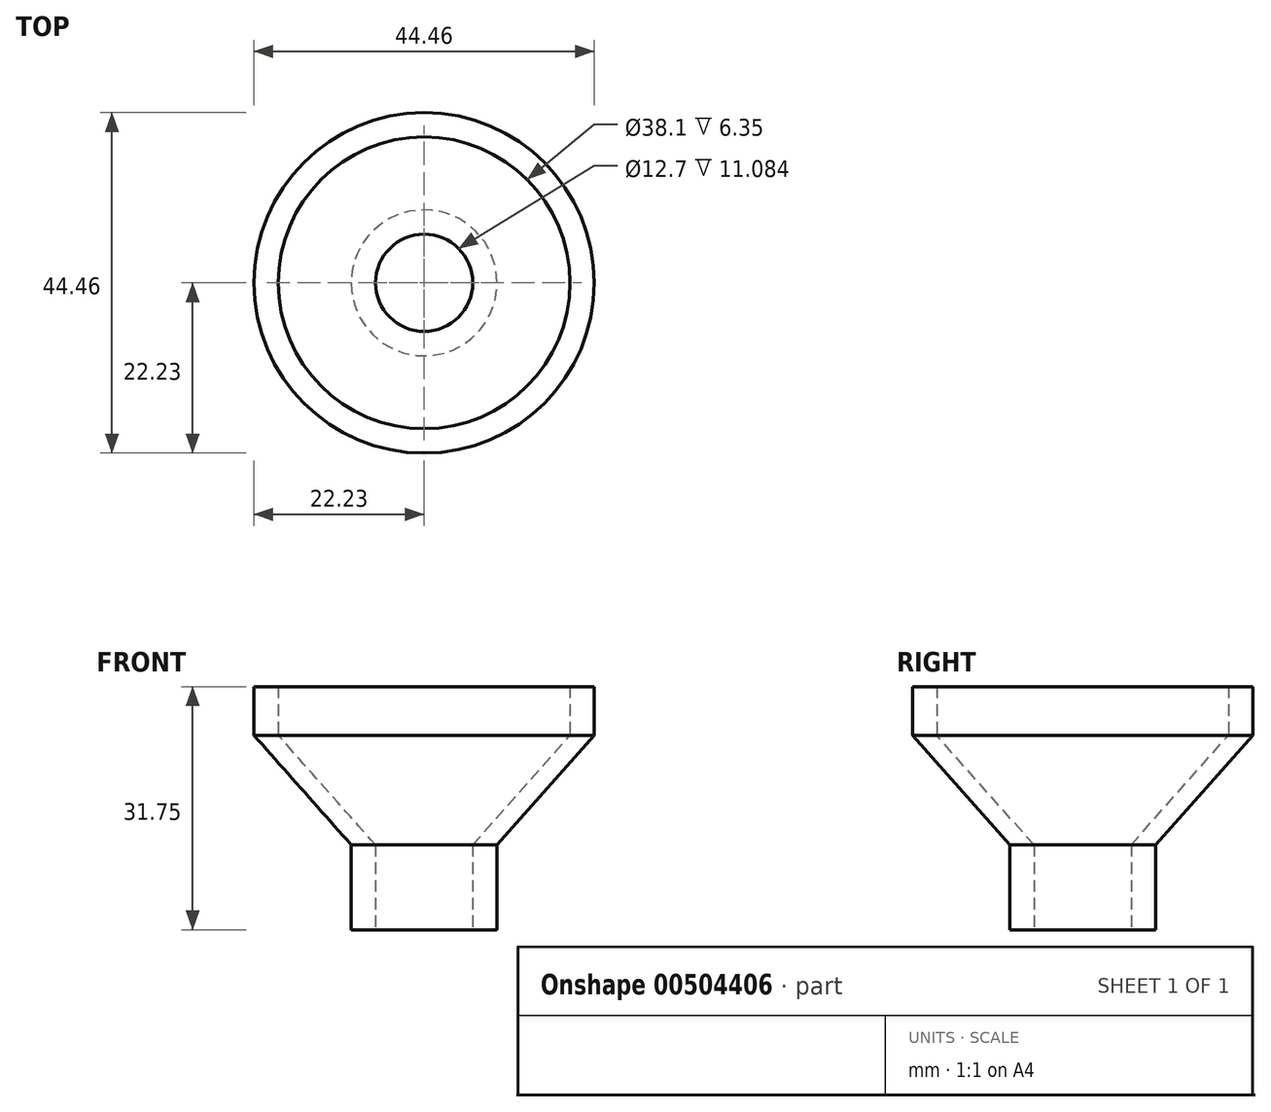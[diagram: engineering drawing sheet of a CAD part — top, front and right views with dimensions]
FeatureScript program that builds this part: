
annotation { "Feature Type Name" : "Feature", "Feature Type Description" : "" }
export const myFeature = defineFeature(function(context is Context, id is Id, definition is map)
    precondition{}
    {
        {
            var Q0;
            Q0=qCreatedBy(makeId("Right.planeOp"),FACE);
            var sketch = newSketch(context, id + "F0", { "sketchPlane" : qUnion([Q0])});
            skLineSegment(sketch, "E0.bottom", {"start": v(22.22, 6.35) * mm, "end": v(19.05, 6.35) * mm});
            skLineSegment(sketch, "E0.top", {"start": v(22.23, 0) * mm, "end": v(19.05, 0) * mm});
            skLineSegment(sketch, "E0.left", {"start": v(22.23, 6.35) * mm, "end": v(22.23, 0) * mm});
            skLineSegment(sketch, "E0.right", {"start": v(19.05, 6.35) * mm, "end": v(19.05, 0) * mm});
            skLineSegment(sketch, "E1.bottom", {"start": v(9.52, -14.32) * mm, "end": v(6.35, -14.32) * mm});
            skLineSegment(sketch, "E1.top", {"start": v(9.53, -25.4) * mm, "end": v(6.35, -25.4) * mm});
            skLineSegment(sketch, "E1.left", {"start": v(9.52, -14.32) * mm, "end": v(9.53, -25.4) * mm});
            skLineSegment(sketch, "E1.right", {"start": v(6.35, -14.32) * mm, "end": v(6.35, -25.4) * mm});
            skLineSegment(sketch, "E2", {"start": v(6.35, -25.4) * mm, "end": v(9.53, -25.4) * mm});
            skLineSegment(sketch, "E3", {"start": v(22.23, 0) * mm, "end": v(9.52, -14.32) * mm});
            skLineSegment(sketch, "E4", {"start": v(19.05, 0) * mm, "end": v(6.35, -14.32) * mm});
            skLineSegment(sketch, "E5", {"start": v(6.35, -25.4) * mm, "end": v(0, -25.4) * mm});
            skLineSegment(sketch, "E6", {"start": v(0, -25.4) * mm, "end": v(0, -18.22) * mm});
            skSolve(sketch);
        }
        {
            var Q0;
            Q0=makeQuery(id+"F0.imprint","IMPRINT",FACE,{"disambiguationData":[TD([[makeQuery(id+"F0.imprint","IMPRINT",EDGE,{"derivedFrom":sQuery(id+"F0.wireOp",EDGE,"E0.bottom")}),1.0]])]});
            var Q1;
            Q1=makeQuery(id+"F0.imprint","IMPRINT",FACE,{"disambiguationData":[TD([[makeQuery(id+"F0.imprint","IMPRINT",EDGE,{"derivedFrom":sQuery(id+"F0.wireOp",EDGE,"E0.top")}),1.0]])]});
            var Q2;
            Q2=makeQuery(id+"F0.imprint","IMPRINT",FACE,{"disambiguationData":[TD([[makeQuery(id+"F0.imprint","IMPRINT",EDGE,{"derivedFrom":sQuery(id+"F0.wireOp",EDGE,"E1.bottom")}),1.0]])]});
            var Q3;
            Q3=sQuery(id+"F0.wireOp",EDGE,"E6");
            revolve(context, id + "F1", {"entities" : qUnion([Q0, Q1, Q2]), "axis" : qUnion([Q3]), "revolveType" : RevolveType.FULL});
        }
        {
            var Q0;
            Q0=qCreatedBy(makeId("Top.planeOp"),FACE);
            var sketch = newSketch(context, id + "F2", { "sketchPlane" : qUnion([Q0])});
            skCircle(sketch, "E7", {"center": v(0, 0) * mm, "radius": 9.04 * mm});
            skSolve(sketch);
        }
        {
            var Q0;
            Q0 = qSketchRegion(id + "F2", true);
            extrude(context, id + "F3", {"entities" : qUnion([Q0]), "depth" : 9.52 * mm, "offsetDistance" : 25.4 * mm});
        }
        {
            var Q0;
            Q0=qCreatedBy(makeId("Top.planeOp"),FACE);
            var sketch = newSketch(context, id + "F4", { "sketchPlane" : qUnion([Q0])});
            skCircle(sketch, "E8", {"center": v(0, 0) * mm, "radius": 9.54 * mm});
            skSolve(sketch);
        }
        {
            var Q0;
            Q0=makeQuery(id+"F4.imprint","IMPRINT",FACE,{"disambiguationData":[TD([[makeQuery(id+"F4.imprint","IMPRINT",EDGE,{"derivedFrom":sQuery(id+"F4.wireOp",EDGE,"E8")}),1.0]])]});
            extrude(context, id + "F5", {"entities" : qUnion([Q0]), "operationType" : NewBodyOperationType.ADD, "depth" : 25.4 * mm, "offsetDistance" : 25.4 * mm});
        }
        {
            var Q0;
            Q0=makeQuery(id+"F3.opExtrude","SWEPT_BODY",BODY,{"disambiguationData":[OSD([sQuery(id+"F2.wireOp",EDGE,"E7")])]});
            deleteBodies(context, id + "F6", {"entities" : qUnion([Q0])});
        }
    });
